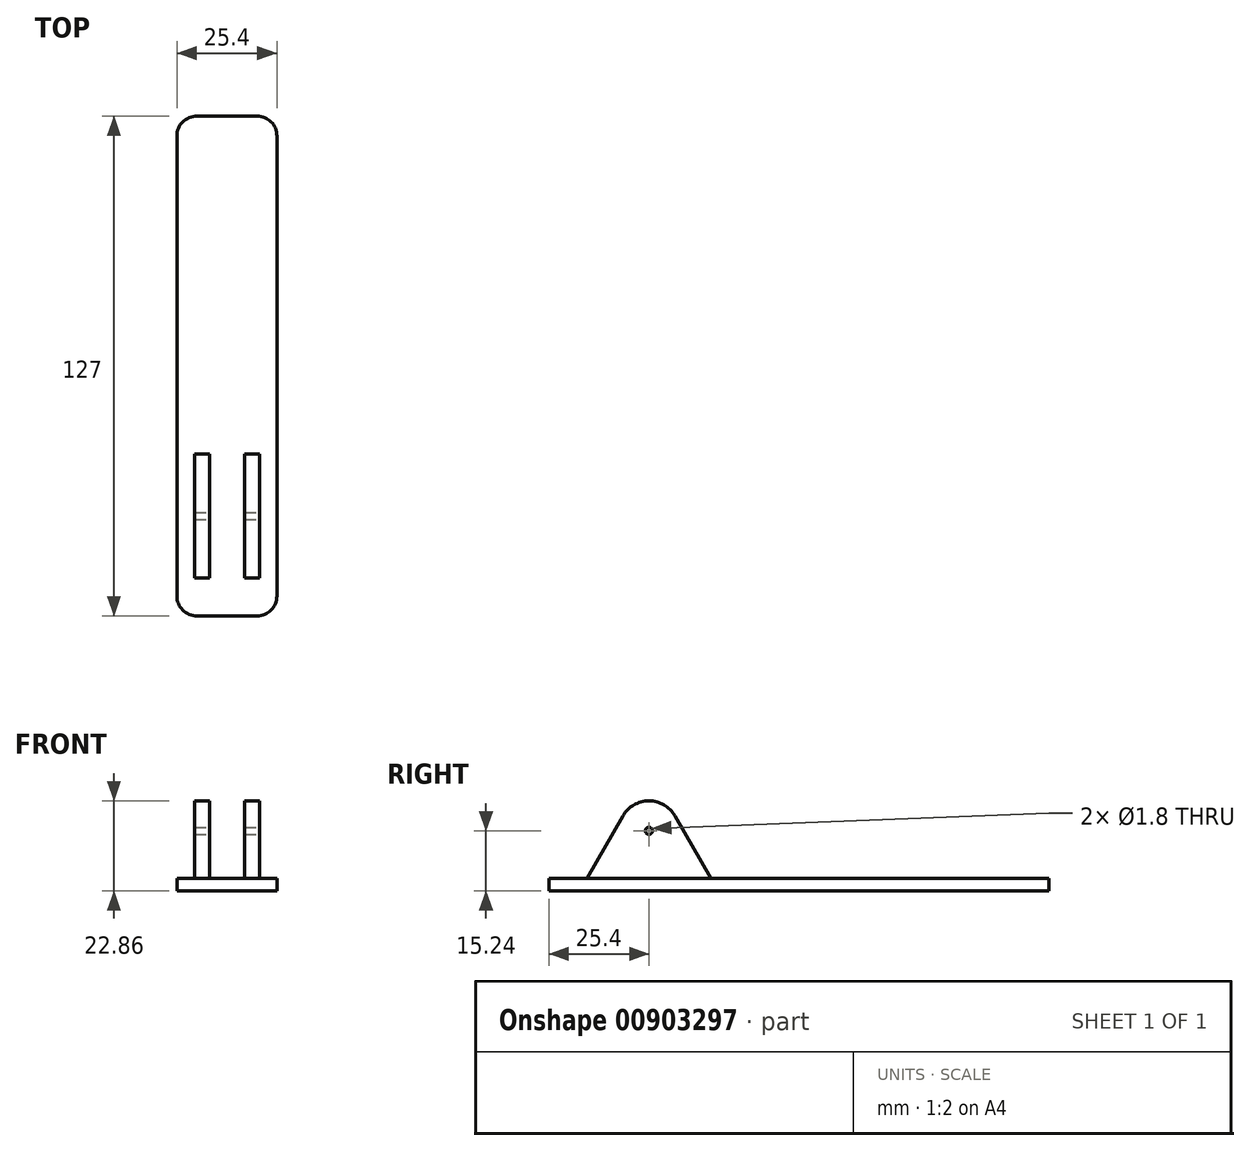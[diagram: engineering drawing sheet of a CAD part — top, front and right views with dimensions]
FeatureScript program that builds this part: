
annotation { "Feature Type Name" : "Feature", "Feature Type Description" : "" }
export const myFeature = defineFeature(function(context is Context, id is Id, definition is map)
    precondition{}
    {
        {
            var Q0;
            Q0=qCreatedBy(makeId("Top.planeOp"),FACE);
            var sketch = newSketch(context, id + "F0", { "sketchPlane" : qUnion([Q0])});
            skLineSegment(sketch, "E0.bottom", {"start": v(12.7, 63.5) * mm, "end": v(-12.7, 63.5) * mm});
            skLineSegment(sketch, "E0.top", {"start": v(12.7, -63.5) * mm, "end": v(-12.7, -63.5) * mm});
            skLineSegment(sketch, "E0.left", {"start": v(12.7, 63.5) * mm, "end": v(12.7, -63.5) * mm});
            skLineSegment(sketch, "E0.right", {"start": v(-12.7, 63.5) * mm, "end": v(-12.7, -63.5) * mm});
            skPoint(sketch, "E0.middle", {"position": v(0, 0) * mm});
            skSolve(sketch);
        }
        {
            var Q0;
            Q0=makeQuery(id+"F0.imprint","IMPRINT",FACE,{"disambiguationData":[TD([[makeQuery(id+"F0.imprint","IMPRINT",EDGE,{"derivedFrom":sQuery(id+"F0.wireOp",EDGE,"E0.bottom")}),1.0]])]});
            extrude(context, id + "F1", {"entities" : qUnion([Q0]), "depth" : 3.17 * mm, "offsetDistance" : 25.4 * mm});
        }
        {
            var Q0;
            Q0=qCreatedBy(makeId("Right.planeOp"),FACE);
            var sketch = newSketch(context, id + "F2", { "sketchPlane" : qUnion([Q0])});
            skCircle(sketch, "E1", {"center": v(-38.1, 15.24) * mm, "radius": 9.53 * mm, "construction": true});
            skCircle(sketch, "E2", {"center": v(38.1, 15.24) * mm, "radius": 9.53 * mm, "construction": true});
            skLineSegment(sketch, "E3", {"start": v(-38.1, 15.24) * mm, "end": v(38.1, 15.24) * mm, "construction": true});
            skLineSegment(sketch, "E4", {"start": v(0, 15.24) * mm, "end": v(0, 0) * mm, "construction": true});
            skLineSegment(sketch, "E5", {"start": v(-53.86, 3.17) * mm, "end": v(-44.7, 19.05) * mm});
            skLineSegment(sketch, "E6", {"start": v(-31.5, 19.05) * mm, "end": v(-22.34, 3.17) * mm});
            skLineSegment(sketch, "E7", {"start": v(-22.34, 3.18) * mm, "end": v(-53.86, 3.18) * mm});
            skLineSegment(sketch, "E8", {"start": v(-38.1, 3.18) * mm, "end": v(-38.1, 20.96) * mm, "construction": true});
            skArc(sketch, "E9", {"start": v(-31.5, 19.05) * mm, "mid": v(-38.1, 22.86) * mm, "end": v(-44.7, 19.05) * mm});
            skCircle(sketch, "E10", {"center": v(-38.1, 15.24) * mm, "radius": 0.87 * mm, "construction": true});
            skCircle(sketch, "E11", {"center": v(-38.1, 15.24) * mm, "radius": 6.99 * mm, "construction": true});
            skCircle(sketch, "E12", {"center": v(38.1, 15.24) * mm, "radius": 6.99 * mm, "construction": true});
            skCircle(sketch, "E13", {"center": v(0, 143.7) * mm, "radius": 127 * mm, "construction": true});
            skCircle(sketch, "E14", {"center": v(0, 89.19) * mm, "radius": 76.2 * mm, "construction": true});
            skSolve(sketch);
        }
        {
            var Q0;
            Q0 = qSketchRegion(id + "F2", true);
            extrude(context, id + "F3", {"entities" : qUnion([Q0]), "operationType" : NewBodyOperationType.ADD, "endBound" : BoundingType.SYMMETRIC, "depth" : 16.5 * mm, "offsetDistance" : 25.4 * mm});
        }
        {
            var Q0;
            Q0 = qSketchRegion(id + "F2", true);
            extrude(context, id + "F4", {"entities" : qUnion([Q0]), "operationType" : NewBodyOperationType.REMOVE, "endBound" : BoundingType.SYMMETRIC, "oppositeDirection" : true, "depth" : 8.9 * mm, "offsetDistance" : 25.4 * mm});
        }
        {
            var Q0;
            Q0=makeQuery(id+"F3.opExtrude","CAP_FACE",FACE,{"disambiguationData":[OSD([sQuery(id+"F2.wireOp",EDGE,"E5"),sQuery(id+"F2.wireOp",EDGE,"E6"),sQuery(id+"F2.wireOp",EDGE,"E7"),sQuery(id+"F2.wireOp",EDGE,"E9")])],"isStart":false});
            var sketch = newSketch(context, id + "F5", { "sketchPlane" : qUnion([Q0])});
            skCircle(sketch, "E15", {"center": v(-38.1, 15.24) * mm, "radius": 0.9 * mm});
            skSolve(sketch);
        }
        {
            var Q0;
            Q0 = qSketchRegion(id + "F5", true);
            extrude(context, id + "F6", {"entities" : qUnion([Q0]), "operationType" : NewBodyOperationType.REMOVE, "endBound" : BoundingType.THROUGH_ALL, "oppositeDirection" : true, "depth" : 25.4 * mm, "offsetDistance" : 25.4 * mm});
        }
        {
            var Q0;
            Q0=makeQuery(id+"F1.opExtrude","SWEPT_EDGE",EDGE,{"disambiguationData":[OSD([sQuery(id+"F0.wireOp",EDGE,"E0.top"),sQuery(id+"F0.wireOp",EDGE,"E0.left")])]});
            var Q1;
            Q1=makeQuery(id+"F1.opExtrude","SWEPT_EDGE",EDGE,{"disambiguationData":[OSD([sQuery(id+"F0.wireOp",EDGE,"E0.top"),sQuery(id+"F0.wireOp",EDGE,"E0.right")])]});
            var Q2;
            Q2=makeQuery(id+"F1.opExtrude","SWEPT_EDGE",EDGE,{"disambiguationData":[OSD([sQuery(id+"F0.wireOp",EDGE,"E0.bottom"),sQuery(id+"F0.wireOp",EDGE,"E0.left")])]});
            var Q3;
            Q3=makeQuery(id+"F1.opExtrude","SWEPT_EDGE",EDGE,{"disambiguationData":[OSD([sQuery(id+"F0.wireOp",EDGE,"E0.bottom"),sQuery(id+"F0.wireOp",EDGE,"E0.right")])]});
            fillet(context, id + "F7", {"entities" : qUnion([Q0, Q1, Q2, Q3]), "radius" : 5.08 * mm, "tangentPropagation" : true, "allowEdgeOverflow" : false});
        }
    });
